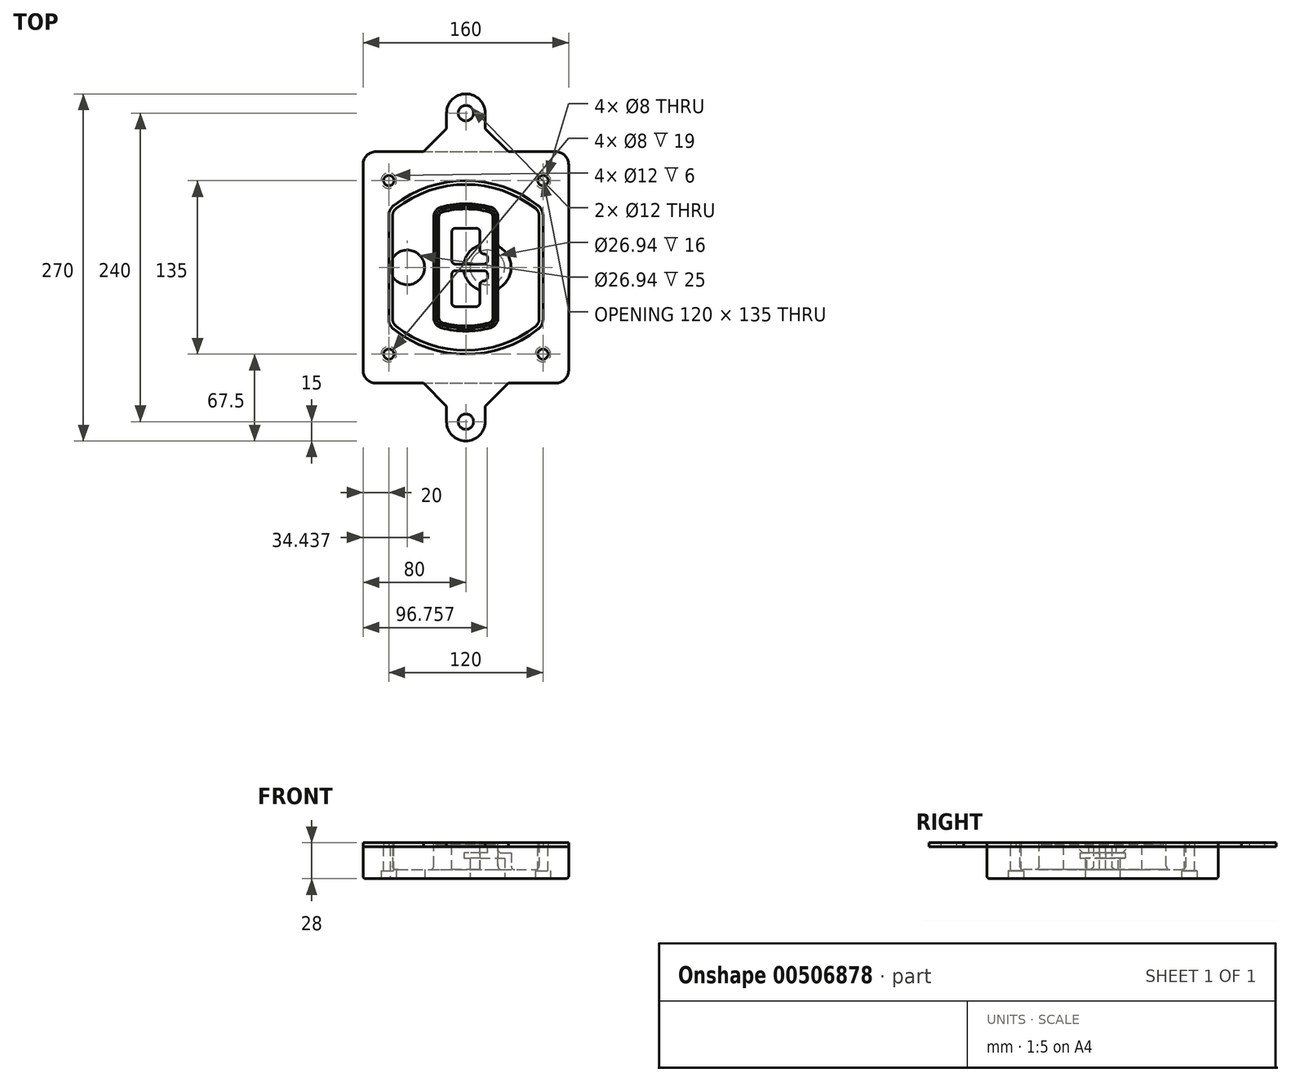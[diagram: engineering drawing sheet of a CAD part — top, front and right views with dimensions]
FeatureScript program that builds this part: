
annotation { "Feature Type Name" : "Feature", "Feature Type Description" : "" }
export const myFeature = defineFeature(function(context is Context, id is Id, definition is map)
    precondition{}
    {
        {
            var Q0;
            Q0=qCreatedBy(makeId("Top.planeOp"),FACE);
            var sketch = newSketch(context, id + "F0", { "sketchPlane" : qUnion([Q0])});
            skPoint(sketch, "E0.rect.middle", {"position": v(0, 0) * mm});
            skLineSegment(sketch, "E1.bottom", {"start": v(-70, -90) * mm, "end": v(70, -90) * mm});
            skLineSegment(sketch, "E1.top", {"start": v(-70, 90) * mm, "end": v(70, 90) * mm});
            skLineSegment(sketch, "E1.left", {"start": v(-80, -80) * mm, "end": v(-80, 80) * mm});
            skLineSegment(sketch, "E1.right", {"start": v(80, -80) * mm, "end": v(80, 80) * mm});
            skLineSegment(sketch, "E2", {"start": v(-80, 90) * mm, "end": v(80, -90) * mm, "construction": true});
            skLineSegment(sketch, "E3", {"start": v(80, 90) * mm, "end": v(-80, -90) * mm, "construction": true});
            skCircle(sketch, "E4", {"center": v(-60, 67.5) * mm, "radius": 4 * mm});
            skCircle(sketch, "E5", {"center": v(60, 67.5) * mm, "radius": 4 * mm});
            skCircle(sketch, "E6", {"center": v(60, -67.5) * mm, "radius": 4 * mm});
            skCircle(sketch, "E7", {"center": v(-60, -67.5) * mm, "radius": 4 * mm});
            skLineSegment(sketch, "E8", {"start": v(-60, 67.5) * mm, "end": v(60, 67.5) * mm, "construction": true});
            skLineSegment(sketch, "E9", {"start": v(60, 67.5) * mm, "end": v(60, -67.5) * mm, "construction": true});
            skLineSegment(sketch, "E10", {"start": v(60, -67.5) * mm, "end": v(-60, -67.5) * mm, "construction": true});
            skLineSegment(sketch, "E11", {"start": v(-60, -67.5) * mm, "end": v(-60, 67.5) * mm, "construction": true});
            skLineSegment(sketch, "E12", {"start": v(-60, 40.3) * mm, "end": v(-60, -40.3) * mm});
            skLineSegment(sketch, "E13", {"start": v(60, 40.3) * mm, "end": v(60, -40.3) * mm});
            skArc(sketch, "E14", {"start": v(56.15, 48.18) * mm, "mid": v(0, 67.5) * mm, "end": v(-56.15, 48.18) * mm});
            skArc(sketch, "E15", {"start": v(-56.15, -48.18) * mm, "mid": v(0, -67.5) * mm, "end": v(56.15, -48.18) * mm});
            skLineSegment(sketch, "E16", {"start": v(-60, 0) * mm, "end": v(60, 0) * mm, "construction": true});
            skPoint(sketch, "E17.visualSharp", {"position": v(-60, -45) * mm});
            skArc(sketch, "E17.filletArc", {"start": v(-60, -40.3) * mm, "mid": v(-58.99, -44.68) * mm, "end": v(-56.15, -48.18) * mm});
            skPoint(sketch, "E18.visualSharp", {"position": v(-60, 45) * mm});
            skArc(sketch, "E18.filletArc", {"start": v(-56.15, 48.18) * mm, "mid": v(-58.99, 44.68) * mm, "end": v(-60, 40.3) * mm});
            skPoint(sketch, "E19.visualSharp", {"position": v(60, 45) * mm});
            skArc(sketch, "E19.filletArc", {"start": v(60, 40.3) * mm, "mid": v(58.99, 44.68) * mm, "end": v(56.15, 48.18) * mm});
            skPoint(sketch, "E20.visualSharp", {"position": v(60, -45) * mm});
            skArc(sketch, "E20.filletArc", {"start": v(56.15, -48.18) * mm, "mid": v(58.99, -44.68) * mm, "end": v(60, -40.3) * mm});
            skPoint(sketch, "E21.visualSharp", {"position": v(-80, 90) * mm});
            skArc(sketch, "E21.filletArc", {"start": v(-70, 90) * mm, "mid": v(-77.07, 87.07) * mm, "end": v(-80, 80) * mm});
            skPoint(sketch, "E22.visualSharp", {"position": v(80, 90) * mm});
            skArc(sketch, "E22.filletArc", {"start": v(80, 80) * mm, "mid": v(77.07, 87.07) * mm, "end": v(70, 90) * mm});
            skPoint(sketch, "E23.visualSharp", {"position": v(80, -90) * mm});
            skArc(sketch, "E23.filletArc", {"start": v(70, -90) * mm, "mid": v(77.07, -87.07) * mm, "end": v(80, -80) * mm});
            skPoint(sketch, "E24.visualSharp", {"position": v(-80, -90) * mm});
            skArc(sketch, "E24.filletArc", {"start": v(-80, -80) * mm, "mid": v(-77.07, -87.07) * mm, "end": v(-70, -90) * mm});
            skArc(sketch, "E25.0", {"start": v(57, 40.3) * mm, "mid": v(56.3, 43.36) * mm, "end": v(54.3, 45.81) * mm});
            skLineSegment(sketch, "E25.1", {"start": v(57, 40.3) * mm, "end": v(57, -40.3) * mm});
            skArc(sketch, "E25.2", {"start": v(54.3, -45.81) * mm, "mid": v(56.3, -43.36) * mm, "end": v(57, -40.3) * mm});
            skArc(sketch, "E25.3", {"start": v(-54.3, -45.81) * mm, "mid": v(0, -64.5) * mm, "end": v(54.3, -45.81) * mm});
            skArc(sketch, "E25.4", {"start": v(-57, -40.3) * mm, "mid": v(-56.3, -43.36) * mm, "end": v(-54.3, -45.81) * mm});
            skArc(sketch, "E25.5", {"start": v(54.3, 45.81) * mm, "mid": v(0, 64.5) * mm, "end": v(-54.3, 45.81) * mm});
            skLineSegment(sketch, "E25.6", {"start": v(-57, 40.3) * mm, "end": v(-57, -40.3) * mm});
            skArc(sketch, "E25.7", {"start": v(-54.3, 45.81) * mm, "mid": v(-56.3, 43.36) * mm, "end": v(-57, 40.3) * mm});
            skArc(sketch, "E26.0", {"start": v(-58.62, 51.33) * mm, "mid": v(-62.58, 46.43) * mm, "end": v(-64, 40.3) * mm});
            skArc(sketch, "E26.1", {"start": v(58.62, 51.33) * mm, "mid": v(0, 71.5) * mm, "end": v(-58.62, 51.33) * mm});
            skArc(sketch, "E26.2", {"start": v(64, 40.3) * mm, "mid": v(62.58, 46.43) * mm, "end": v(58.62, 51.33) * mm});
            skLineSegment(sketch, "E26.3", {"start": v(64, 40.3) * mm, "end": v(64, -40.3) * mm});
            skArc(sketch, "E26.4", {"start": v(58.62, -51.33) * mm, "mid": v(62.58, -46.43) * mm, "end": v(64, -40.3) * mm});
            skLineSegment(sketch, "E26.5", {"start": v(-64, 40.3) * mm, "end": v(-64, -40.3) * mm});
            skArc(sketch, "E26.6", {"start": v(-58.62, -51.33) * mm, "mid": v(0, -71.5) * mm, "end": v(58.62, -51.33) * mm});
            skArc(sketch, "E26.7", {"start": v(-64, -40.3) * mm, "mid": v(-62.58, -46.43) * mm, "end": v(-58.62, -51.33) * mm});
            skSolve(sketch);
        }
        {
            var Q0;
            Q0=makeQuery(id+"F0.imprint","IMPRINT",FACE,{"disambiguationData":[TD([[makeQuery(id+"F0.imprint","IMPRINT",EDGE,{"derivedFrom":sQuery(id+"F0.wireOp",EDGE,"E1.bottom")}),1.0]])]});
            var Q1;
            Q1=makeQuery(id+"F0.imprint","IMPRINT",FACE,{"disambiguationData":[TD([[makeQuery(id+"F0.imprint","IMPRINT",EDGE,{"derivedFrom":sQuery(id+"F0.wireOp",EDGE,"E12")}),1.0]])]});
            var Q2;
            Q2=makeQuery(id+"F0.imprint","IMPRINT",FACE,{"disambiguationData":[TD([[makeQuery(id+"F0.imprint","IMPRINT",EDGE,{"derivedFrom":sQuery(id+"F0.wireOp",EDGE,"E25.0")}),1.0]])]});
            var Q3;
            Q3=makeQuery(id+"F0.imprint","IMPRINT",FACE,{"disambiguationData":[TD([[makeQuery(id+"F0.imprint","IMPRINT",EDGE,{"derivedFrom":sQuery(id+"F0.wireOp",EDGE,"E12")}),-1.0]])]});
            extrude(context, id + "F1", {"entities" : qUnion([Q0, Q1, Q2, Q3]), "oppositeDirection" : true, "depth" : 25 * mm});
        }
        {
            var Q0;
            Q0=makeQuery(id+"F0.imprint","IMPRINT",FACE,{"disambiguationData":[TD([[makeQuery(id+"F0.imprint","IMPRINT",EDGE,{"derivedFrom":sQuery(id+"F0.wireOp",EDGE,"E12")}),1.0]])]});
            extrude(context, id + "F2", {"entities" : qUnion([Q0]), "operationType" : NewBodyOperationType.ADD, "depth" : 3 * mm});
        }
        {
            var Q0;
            Q0=makeQuery(id+"F0.imprint","IMPRINT",FACE,{"disambiguationData":[TD([[makeQuery(id+"F0.imprint","IMPRINT",EDGE,{"derivedFrom":sQuery(id+"F0.wireOp",EDGE,"E25.0")}),1.0]])]});
            extrude(context, id + "F3", {"entities" : qUnion([Q0]), "operationType" : NewBodyOperationType.REMOVE, "oppositeDirection" : true, "depth" : 18 * mm});
        }
        {
            var Q0;
            Q0=makeQuery(id+"F2.opExtrude","CAP_FACE",FACE,{"disambiguationData":[OSD([sQuery(id+"F0.wireOp",EDGE,"E12"),sQuery(id+"F0.wireOp",EDGE,"E13"),sQuery(id+"F0.wireOp",EDGE,"E14"),sQuery(id+"F0.wireOp",EDGE,"E15"),sQuery(id+"F0.wireOp",EDGE,"E17.filletArc"),sQuery(id+"F0.wireOp",EDGE,"E18.filletArc"),sQuery(id+"F0.wireOp",EDGE,"E19.filletArc"),sQuery(id+"F0.wireOp",EDGE,"E20.filletArc"),sQuery(id+"F0.wireOp",EDGE,"E25.0"),sQuery(id+"F0.wireOp",EDGE,"E25.1"),sQuery(id+"F0.wireOp",EDGE,"E25.2"),sQuery(id+"F0.wireOp",EDGE,"E25.3"),sQuery(id+"F0.wireOp",EDGE,"E25.4"),sQuery(id+"F0.wireOp",EDGE,"E25.5"),sQuery(id+"F0.wireOp",EDGE,"E25.6"),sQuery(id+"F0.wireOp",EDGE,"E25.7")])],"isStart":false});
            var sketch = newSketch(context, id + "F4", { "sketchPlane" : qUnion([Q0])});
            skArc(sketch, "E27.0", {"start": v(-19.08, -46.97) * mm, "mid": v(0, -49.5) * mm, "end": v(19.08, -46.97) * mm});
            skArc(sketch, "E28.0", {"start": v(19.08, 46.97) * mm, "mid": v(0, 49.5) * mm, "end": v(-19.08, 46.97) * mm});
            skLineSegment(sketch, "E29", {"start": v(-25, 39.25) * mm, "end": v(-25, -39.25) * mm});
            skLineSegment(sketch, "E30", {"start": v(25, 39.25) * mm, "end": v(25, -39.25) * mm});
            skLineSegment(sketch, "E31", {"start": v(-25, 45.1) * mm, "end": v(25, 45.1) * mm, "construction": true});
            skLineSegment(sketch, "E32", {"start": v(-25, -45.1) * mm, "end": v(25, -45.1) * mm, "construction": true});
            skPoint(sketch, "E33.visualSharp", {"position": v(-25, 45.1) * mm});
            skArc(sketch, "E33.filletArc", {"start": v(-19.08, 46.97) * mm, "mid": v(-23.35, 44.11) * mm, "end": v(-25, 39.25) * mm});
            skPoint(sketch, "E34.visualSharp", {"position": v(25, 45.1) * mm});
            skArc(sketch, "E34.filletArc", {"start": v(25, 39.25) * mm, "mid": v(23.35, 44.11) * mm, "end": v(19.08, 46.97) * mm});
            skPoint(sketch, "E35.visualSharp", {"position": v(25, -45.1) * mm});
            skArc(sketch, "E35.filletArc", {"start": v(19.08, -46.97) * mm, "mid": v(23.35, -44.11) * mm, "end": v(25, -39.25) * mm});
            skPoint(sketch, "E36.visualSharp", {"position": v(-25, -45.1) * mm});
            skArc(sketch, "E36.filletArc", {"start": v(-25, -39.25) * mm, "mid": v(-23.35, -44.11) * mm, "end": v(-19.08, -46.97) * mm});
            skArc(sketch, "E37.0", {"start": v(54.3, 45.81) * mm, "mid": v(0, 64.5) * mm, "end": v(-54.3, 45.81) * mm});
            skArc(sketch, "E37.1", {"start": v(-54.3, 45.81) * mm, "mid": v(-56.3, 43.36) * mm, "end": v(-57, 40.3) * mm});
            skLineSegment(sketch, "E37.2", {"start": v(-57, 40.3) * mm, "end": v(-57, -40.3) * mm});
            skArc(sketch, "E37.3", {"start": v(-57, -40.3) * mm, "mid": v(-56.3, -43.36) * mm, "end": v(-54.3, -45.81) * mm});
            skArc(sketch, "E37.4", {"start": v(-54.3, -45.81) * mm, "mid": v(0, -64.5) * mm, "end": v(54.3, -45.81) * mm});
            skArc(sketch, "E37.5", {"start": v(54.3, -45.81) * mm, "mid": v(56.3, -43.36) * mm, "end": v(57, -40.3) * mm});
            skLineSegment(sketch, "E37.6", {"start": v(57, 40.3) * mm, "end": v(57, -40.3) * mm});
            skArc(sketch, "E37.7", {"start": v(57, 40.3) * mm, "mid": v(56.3, 43.36) * mm, "end": v(54.3, 45.81) * mm});
            skLineSegment(sketch, "E38.0", {"start": v(23, 39.25) * mm, "end": v(23, -39.25) * mm});
            skArc(sketch, "E38.1", {"start": v(18.56, -45.04) * mm, "mid": v(21.76, -42.9) * mm, "end": v(23, -39.25) * mm});
            skArc(sketch, "E38.2", {"start": v(-18.56, -45.04) * mm, "mid": v(0, -47.5) * mm, "end": v(18.56, -45.04) * mm});
            skArc(sketch, "E38.3", {"start": v(-23, -39.25) * mm, "mid": v(-21.76, -42.9) * mm, "end": v(-18.56, -45.04) * mm});
            skLineSegment(sketch, "E38.4", {"start": v(-23, 39.25) * mm, "end": v(-23, -39.25) * mm});
            skArc(sketch, "E38.5", {"start": v(23, 39.25) * mm, "mid": v(21.76, 42.9) * mm, "end": v(18.56, 45.04) * mm});
            skArc(sketch, "E38.6", {"start": v(-18.56, 45.04) * mm, "mid": v(-21.76, 42.9) * mm, "end": v(-23, 39.25) * mm});
            skArc(sketch, "E38.7", {"start": v(18.56, 45.04) * mm, "mid": v(0, 47.5) * mm, "end": v(-18.56, 45.04) * mm});
            skArc(sketch, "E39.0", {"start": v(21, 39.25) * mm, "mid": v(20.18, 41.68) * mm, "end": v(18.04, 43.1) * mm});
            skLineSegment(sketch, "E39.1", {"start": v(21, 39.25) * mm, "end": v(21, -39.25) * mm});
            skArc(sketch, "E39.2", {"start": v(18.04, -43.1) * mm, "mid": v(20.18, -41.68) * mm, "end": v(21, -39.25) * mm});
            skArc(sketch, "E39.3", {"start": v(-18.04, -43.1) * mm, "mid": v(0, -45.5) * mm, "end": v(18.04, -43.1) * mm});
            skArc(sketch, "E39.4", {"start": v(-21, -39.25) * mm, "mid": v(-20.18, -41.68) * mm, "end": v(-18.04, -43.1) * mm});
            skArc(sketch, "E39.5", {"start": v(18.04, 43.1) * mm, "mid": v(0, 45.5) * mm, "end": v(-18.04, 43.1) * mm});
            skLineSegment(sketch, "E39.6", {"start": v(-21, 39.25) * mm, "end": v(-21, -39.25) * mm});
            skArc(sketch, "E39.7", {"start": v(-18.04, 43.1) * mm, "mid": v(-20.18, 41.68) * mm, "end": v(-21, 39.25) * mm});
            skLineSegment(sketch, "E40", {"start": v(-25, 0) * mm, "end": v(25, 0) * mm, "construction": true});
            skLineSegment(sketch, "E41", {"start": v(-11, 5.5) * mm, "end": v(-11, 27.5) * mm});
            skLineSegment(sketch, "E42", {"start": v(-8, 30.5) * mm, "end": v(8, 30.5) * mm});
            skLineSegment(sketch, "E43", {"start": v(11, 27.5) * mm, "end": v(11, 13.5) * mm});
            skLineSegment(sketch, "E44", {"start": v(14, 10.5) * mm, "end": v(14, 10.5) * mm});
            skLineSegment(sketch, "E45", {"start": v(17, 7.5) * mm, "end": v(17, 5.5) * mm});
            skLineSegment(sketch, "E46", {"start": v(14, 2.5) * mm, "end": v(-8, 2.5) * mm});
            skPoint(sketch, "E47.visualSharp", {"position": v(-11, 30.5) * mm});
            skArc(sketch, "E47.filletArc", {"start": v(-8, 30.5) * mm, "mid": v(-10.12, 29.62) * mm, "end": v(-11, 27.5) * mm});
            skPoint(sketch, "E48.visualSharp", {"position": v(11, 30.5) * mm});
            skArc(sketch, "E48.filletArc", {"start": v(11, 27.5) * mm, "mid": v(10.12, 29.62) * mm, "end": v(8, 30.5) * mm});
            skPoint(sketch, "E49.visualSharp", {"position": v(11, 10.5) * mm});
            skArc(sketch, "E49.filletArc", {"start": v(11, 13.5) * mm, "mid": v(11.88, 11.38) * mm, "end": v(14, 10.5) * mm});
            skPoint(sketch, "E50.visualSharp", {"position": v(17, 10.5) * mm});
            skArc(sketch, "E50.filletArc", {"start": v(17, 7.5) * mm, "mid": v(16.12, 9.62) * mm, "end": v(14, 10.5) * mm});
            skPoint(sketch, "E51.visualSharp", {"position": v(17, 2.5) * mm});
            skArc(sketch, "E51.filletArc", {"start": v(14, 2.5) * mm, "mid": v(16.12, 3.38) * mm, "end": v(17, 5.5) * mm});
            skPoint(sketch, "E52.visualSharp", {"position": v(-11, 2.5) * mm});
            skArc(sketch, "E52.filletArc", {"start": v(-11, 5.5) * mm, "mid": v(-10.12, 3.38) * mm, "end": v(-8, 2.5) * mm});
            skLineSegment(sketch, "E53.0.MirrorCS", {"start": v(14, -2.5) * mm, "end": v(-8, -2.5) * mm});
            skArc(sketch, "E54.0.MirrorCS", {"start": v(-11, -5.5) * mm, "mid": v(-10.12, -3.38) * mm, "end": v(-8, -2.5) * mm});
            skLineSegment(sketch, "E55.0.MirrorCS", {"start": v(-11, -5.5) * mm, "end": v(-11, -27.5) * mm});
            skArc(sketch, "E56.0.MirrorCS", {"start": v(-8, -30.5) * mm, "mid": v(-10.12, -29.62) * mm, "end": v(-11, -27.5) * mm});
            skLineSegment(sketch, "E57.0.MirrorCS", {"start": v(-8, -30.5) * mm, "end": v(8, -30.5) * mm});
            skArc(sketch, "E58.0.MirrorCS", {"start": v(11, -27.5) * mm, "mid": v(10.12, -29.62) * mm, "end": v(8, -30.5) * mm});
            skLineSegment(sketch, "E59.0.MirrorCS", {"start": v(11, -27.5) * mm, "end": v(11, -13.5) * mm});
            skArc(sketch, "E60.0.MirrorCS", {"start": v(11, -13.5) * mm, "mid": v(11.88, -11.38) * mm, "end": v(14, -10.5) * mm});
            skArc(sketch, "E61.0.MirrorCS", {"start": v(17, -7.5) * mm, "mid": v(16.12, -9.62) * mm, "end": v(14, -10.5) * mm});
            skLineSegment(sketch, "E62.0.MirrorCS", {"start": v(17, -7.5) * mm, "end": v(17, -5.5) * mm});
            skArc(sketch, "E63.0.MirrorCS", {"start": v(14, -2.5) * mm, "mid": v(16.12, -3.38) * mm, "end": v(17, -5.5) * mm});
            skSolve(sketch);
        }
        {
            var Q0;
            Q0=makeQuery(id+"F4.imprint","IMPRINT",FACE,{"disambiguationData":[TD([[makeQuery(id+"F4.imprint","IMPRINT",EDGE,{"derivedFrom":sQuery(id+"F4.wireOp",EDGE,"E27.0")}),1.0]])]});
            var Q1;
            Q1=makeQuery(id+"F4.imprint","IMPRINT",FACE,{"disambiguationData":[TD([[makeQuery(id+"F4.imprint","IMPRINT",EDGE,{"derivedFrom":sQuery(id+"F4.wireOp",EDGE,"E38.0")}),-1.0]])]});
            var Q2;
            Q2=makeQuery(id+"F4.imprint","IMPRINT",FACE,{"disambiguationData":[TD([[makeQuery(id+"F4.imprint","IMPRINT",EDGE,{"derivedFrom":sQuery(id+"F4.wireOp",EDGE,"E39.0")}),1.0]])]});
            extrude(context, id + "F5", {"entities" : qUnion([Q0, Q1, Q2]), "operationType" : NewBodyOperationType.ADD, "endBound" : BoundingType.UP_TO_NEXT, "oppositeDirection" : true, "depth" : 25 * mm});
        }
        {
            var Q0;
            Q0=makeQuery(id+"F4.imprint","IMPRINT",FACE,{"disambiguationData":[TD([[makeQuery(id+"F4.imprint","IMPRINT",EDGE,{"derivedFrom":sQuery(id+"F4.wireOp",EDGE,"E38.0")}),-1.0]])]});
            extrude(context, id + "F6", {"entities" : qUnion([Q0]), "operationType" : NewBodyOperationType.REMOVE, "oppositeDirection" : true, "depth" : 2 * mm});
        }
        {
            var Q0;
            Q0=makeQuery(id+"F1.opExtrude","CAP_FACE",FACE,{"disambiguationData":[OSD([sQuery(id+"F0.wireOp",EDGE,"E1.bottom"),sQuery(id+"F0.wireOp",EDGE,"E1.top"),sQuery(id+"F0.wireOp",EDGE,"E1.left"),sQuery(id+"F0.wireOp",EDGE,"E1.right"),sQuery(id+"F0.wireOp",EDGE,"E4"),sQuery(id+"F0.wireOp",EDGE,"E5"),sQuery(id+"F0.wireOp",EDGE,"E6"),sQuery(id+"F0.wireOp",EDGE,"E7"),sQuery(id+"F0.wireOp",EDGE,"E21.filletArc"),sQuery(id+"F0.wireOp",EDGE,"E22.filletArc"),sQuery(id+"F0.wireOp",EDGE,"E23.filletArc"),sQuery(id+"F0.wireOp",EDGE,"E24.filletArc")])],"isStart":false});
            var sketch = newSketch(context, id + "F7", { "sketchPlane" : qUnion([Q0])});
            skCircle(sketch, "E64", {"center": v(16.76, 0) * mm, "radius": 13.47 * mm});
            skCircle(sketch, "E65", {"center": v(-45.56, 0) * mm, "radius": 13.47 * mm});
            skLineSegment(sketch, "E66", {"start": v(80, 0) * mm, "end": v(-80, 0) * mm});
            skCircle(sketch, "E67", {"center": v(16.76, 0) * mm, "radius": 18.47 * mm});
            skCircle(sketch, "E68", {"center": v(60, -67.5) * mm, "radius": 6 * mm});
            skCircle(sketch, "E69", {"center": v(-60, -67.5) * mm, "radius": 6 * mm});
            skCircle(sketch, "E70", {"center": v(-60, 67.5) * mm, "radius": 6 * mm});
            skCircle(sketch, "E71", {"center": v(60, 67.5) * mm, "radius": 6 * mm});
            skSolve(sketch);
        }
        {
            var Q0;
            {var subQ1=sQuery(id+"F7.wireOp",EDGE,"E66");var subQ4=sQuery(id+"F7.wireOp",EDGE,"E64");var subQ6=makeQuery(id+"F7.imprint","INTERSECT",VERTEX,{"disambiguationData":[OD(0.0)],"derivedFrom":[subQ4,subQ1]});Q0=makeQuery(id+"F7.imprint","IMPRINT",FACE,{"disambiguationData":[TD([[makeQuery(id+"F7.imprint","IMPRINT",EDGE,{"disambiguationData":[TD([[subQ6,-1.0]])],"derivedFrom":subQ4}),-1.0]])]});}
            var Q1;
            {var subQ0=sQuery(id+"F7.wireOp",EDGE,"E66");var subQ1=sQuery(id+"F7.wireOp",EDGE,"E64");var subQ3=makeQuery(id+"F7.imprint","INTERSECT",VERTEX,{"disambiguationData":[OD(0.0)],"derivedFrom":[subQ1,subQ0]});Q1=makeQuery(id+"F7.imprint","IMPRINT",FACE,{"disambiguationData":[TD([[makeQuery(id+"F7.imprint","IMPRINT",EDGE,{"disambiguationData":[TD([[subQ3,-1.0]])],"derivedFrom":subQ1}),1.0]])]});}
            var Q2;
            {var subQ0=sQuery(id+"F7.wireOp",EDGE,"E66");var subQ1=sQuery(id+"F7.wireOp",EDGE,"E64");var subQ3=makeQuery(id+"F7.imprint","INTERSECT",VERTEX,{"disambiguationData":[OD(0.0)],"derivedFrom":[subQ1,subQ0]});Q2=makeQuery(id+"F7.imprint","IMPRINT",FACE,{"disambiguationData":[TD([[makeQuery(id+"F7.imprint","IMPRINT",EDGE,{"disambiguationData":[TD([[subQ3,1.0]])],"derivedFrom":subQ1}),1.0]])]});}
            var Q3;
            {var subQ1=sQuery(id+"F7.wireOp",EDGE,"E66");var subQ4=sQuery(id+"F7.wireOp",EDGE,"E64");var subQ6=makeQuery(id+"F7.imprint","INTERSECT",VERTEX,{"disambiguationData":[OD(0.0)],"derivedFrom":[subQ4,subQ1]});Q3=makeQuery(id+"F7.imprint","IMPRINT",FACE,{"disambiguationData":[TD([[makeQuery(id+"F7.imprint","IMPRINT",EDGE,{"disambiguationData":[TD([[subQ6,1.0]])],"derivedFrom":subQ4}),-1.0]])]});}
            extrude(context, id + "F8", {"entities" : qUnion([Q0, Q1, Q2, Q3]), "operationType" : NewBodyOperationType.ADD, "oppositeDirection" : true, "depth" : 20 * mm});
        }
        {
            var Q0;
            {var subQ0=sQuery(id+"F7.wireOp",EDGE,"E66");var subQ1=sQuery(id+"F7.wireOp",EDGE,"E64");var subQ3=makeQuery(id+"F7.imprint","INTERSECT",VERTEX,{"disambiguationData":[OD(0.0)],"derivedFrom":[subQ1,subQ0]});Q0=makeQuery(id+"F7.imprint","IMPRINT",FACE,{"disambiguationData":[TD([[makeQuery(id+"F7.imprint","IMPRINT",EDGE,{"disambiguationData":[TD([[subQ3,-1.0]])],"derivedFrom":subQ1}),1.0]])]});}
            var Q1;
            {var subQ0=sQuery(id+"F7.wireOp",EDGE,"E66");var subQ1=sQuery(id+"F7.wireOp",EDGE,"E64");var subQ3=makeQuery(id+"F7.imprint","INTERSECT",VERTEX,{"disambiguationData":[OD(0.0)],"derivedFrom":[subQ1,subQ0]});Q1=makeQuery(id+"F7.imprint","IMPRINT",FACE,{"disambiguationData":[TD([[makeQuery(id+"F7.imprint","IMPRINT",EDGE,{"disambiguationData":[TD([[subQ3,1.0]])],"derivedFrom":subQ1}),1.0]])]});}
            extrude(context, id + "F9", {"entities" : qUnion([Q0, Q1]), "operationType" : NewBodyOperationType.REMOVE, "oppositeDirection" : true, "depth" : 16 * mm});
        }
        {
            var Q0;
            {var subQ0=sQuery(id+"F7.wireOp",EDGE,"E66");var subQ1=sQuery(id+"F7.wireOp",EDGE,"E65");var subQ3=makeQuery(id+"F7.imprint","INTERSECT",VERTEX,{"disambiguationData":[OD(0.0)],"derivedFrom":[subQ1,subQ0]});Q0=makeQuery(id+"F7.imprint","IMPRINT",FACE,{"disambiguationData":[TD([[makeQuery(id+"F7.imprint","IMPRINT",EDGE,{"disambiguationData":[TD([[subQ3,-1.0]])],"derivedFrom":subQ1}),1.0]])]});}
            var Q1;
            {var subQ0=sQuery(id+"F7.wireOp",EDGE,"E66");var subQ1=sQuery(id+"F7.wireOp",EDGE,"E65");var subQ3=makeQuery(id+"F7.imprint","INTERSECT",VERTEX,{"disambiguationData":[OD(0.0)],"derivedFrom":[subQ1,subQ0]});Q1=makeQuery(id+"F7.imprint","IMPRINT",FACE,{"disambiguationData":[TD([[makeQuery(id+"F7.imprint","IMPRINT",EDGE,{"disambiguationData":[TD([[subQ3,1.0]])],"derivedFrom":subQ1}),1.0]])]});}
            extrude(context, id + "F10", {"entities" : qUnion([Q0, Q1]), "operationType" : NewBodyOperationType.REMOVE, "oppositeDirection" : true, "depth" : 25 * mm});
        }
        {
            var Q0;
            Q0=makeQuery(id+"F7.imprint","IMPRINT",FACE,{"disambiguationData":[TD([[makeQuery(id+"F7.imprint","IMPRINT",EDGE,{"derivedFrom":sQuery(id+"F7.wireOp",EDGE,"E68")}),1.0]])]});
            var Q1;
            Q1=makeQuery(id+"F7.imprint","IMPRINT",FACE,{"disambiguationData":[TD([[makeQuery(id+"F7.imprint","IMPRINT",EDGE,{"derivedFrom":makeQuery(id+"F1.opExtrude","CAP_EDGE",EDGE,{"disambiguationData":[OSD([sQuery(id+"F0.wireOp",EDGE,"E5")])],"isStart":false})}),-1.0]])]});
            var Q2;
            Q2=makeQuery(id+"F7.imprint","IMPRINT",FACE,{"disambiguationData":[TD([[makeQuery(id+"F7.imprint","IMPRINT",EDGE,{"derivedFrom":sQuery(id+"F7.wireOp",EDGE,"E69")}),1.0]])]});
            var Q3;
            Q3=makeQuery(id+"F7.imprint","IMPRINT",FACE,{"disambiguationData":[TD([[makeQuery(id+"F7.imprint","IMPRINT",EDGE,{"derivedFrom":makeQuery(id+"F1.opExtrude","CAP_EDGE",EDGE,{"disambiguationData":[OSD([sQuery(id+"F0.wireOp",EDGE,"E4")])],"isStart":false})}),-1.0]])]});
            var Q4;
            Q4=makeQuery(id+"F7.imprint","IMPRINT",FACE,{"disambiguationData":[TD([[makeQuery(id+"F7.imprint","IMPRINT",EDGE,{"derivedFrom":sQuery(id+"F7.wireOp",EDGE,"E70")}),1.0]])]});
            var Q5;
            Q5=makeQuery(id+"F7.imprint","IMPRINT",FACE,{"disambiguationData":[TD([[makeQuery(id+"F7.imprint","IMPRINT",EDGE,{"derivedFrom":makeQuery(id+"F1.opExtrude","CAP_EDGE",EDGE,{"disambiguationData":[OSD([sQuery(id+"F0.wireOp",EDGE,"E7")])],"isStart":false})}),-1.0]])]});
            var Q6;
            Q6=makeQuery(id+"F7.imprint","IMPRINT",FACE,{"disambiguationData":[TD([[makeQuery(id+"F7.imprint","IMPRINT",EDGE,{"derivedFrom":sQuery(id+"F7.wireOp",EDGE,"E71")}),1.0]])]});
            var Q7;
            Q7=makeQuery(id+"F7.imprint","IMPRINT",FACE,{"disambiguationData":[TD([[makeQuery(id+"F7.imprint","IMPRINT",EDGE,{"derivedFrom":makeQuery(id+"F1.opExtrude","CAP_EDGE",EDGE,{"disambiguationData":[OSD([sQuery(id+"F0.wireOp",EDGE,"E6")])],"isStart":false})}),-1.0]])]});
            extrude(context, id + "F11", {"entities" : qUnion([Q0, Q1, Q2, Q3, Q4, Q5, Q6, Q7]), "operationType" : NewBodyOperationType.REMOVE, "oppositeDirection" : true, "depth" : 6 * mm});
        }
        {
            var Q0;
            Q0=makeQuery(id+"F9.boolean.opBoolean","COPY",FACE,{"derivedFrom":makeQuery(id+"F9.opExtrude","CAP_FACE",FACE,{"disambiguationData":[OSD([sQuery(id+"F7.wireOp",EDGE,"E64")])],"isStart":false})});
            var sketch = newSketch(context, id + "F12", { "sketchPlane" : qUnion([Q0])});
            skArc(sketch, "E72.0", {"start": v(11, 17.55) * mm, "mid": v(2.57, 11.82) * mm, "end": v(-1.54, 2.5) * mm});
            skArc(sketch, "E72.1", {"start": v(-1.54, -2.5) * mm, "mid": v(2.57, -11.82) * mm, "end": v(11, -17.55) * mm});
            skLineSegment(sketch, "E73", {"start": v(-1.54, -2.5) * mm, "end": v(14, -2.5) * mm});
            skLineSegment(sketch, "E74.0", {"start": v(14, 2.5) * mm, "end": v(-1.54, 2.5) * mm});
            skArc(sketch, "E74.1", {"start": v(14, 2.5) * mm, "mid": v(16.12, 3.38) * mm, "end": v(17, 5.5) * mm});
            skLineSegment(sketch, "E74.2", {"start": v(17, 7.5) * mm, "end": v(17, 5.5) * mm});
            skArc(sketch, "E74.3", {"start": v(17, 7.5) * mm, "mid": v(16.12, 9.62) * mm, "end": v(14, 10.5) * mm});
            skArc(sketch, "E74.4", {"start": v(11, 13.5) * mm, "mid": v(11.88, 11.38) * mm, "end": v(14, 10.5) * mm});
            skLineSegment(sketch, "E74.5", {"start": v(11, 17.55) * mm, "end": v(11, 13.5) * mm});
            skLineSegment(sketch, "E74.7", {"start": v(14, -2.5) * mm, "end": v(-1.54, -2.5) * mm});
            skArc(sketch, "E74.8", {"start": v(14, -2.5) * mm, "mid": v(16.12, -3.38) * mm, "end": v(17, -5.5) * mm});
            skLineSegment(sketch, "E74.9", {"start": v(17, -7.5) * mm, "end": v(17, -5.5) * mm});
            skArc(sketch, "E74.10", {"start": v(17, -7.5) * mm, "mid": v(16.12, -9.62) * mm, "end": v(14, -10.5) * mm});
            skArc(sketch, "E74.11", {"start": v(11, -13.5) * mm, "mid": v(11.88, -11.38) * mm, "end": v(14, -10.5) * mm});
            skLineSegment(sketch, "E74.12", {"start": v(11, -17.55) * mm, "end": v(11, -13.5) * mm});
            skPoint(sketch, "E75.orphan", {"position": v(11, -27.5) * mm});
            skPoint(sketch, "E76.orphan", {"position": v(-8, -2.5) * mm});
            skPoint(sketch, "E77.orphan", {"position": v(-8, 2.5) * mm});
            skPoint(sketch, "E78.orphan", {"position": v(11, 27.5) * mm});
            skSolve(sketch);
        }
        {
            var Q0;
            {var subQ7=sQuery(id+"F12.wireOp",EDGE,"E72.0");var subQ14=sQuery(id+"F12.wireOp",EDGE,"E72.1");var subQ16=sQuery(id+"F12.wireOp",EDGE,"E74.1");var subQ18=sQuery(id+"F12.wireOp",EDGE,"E74.8");Q0=qUnion([makeQuery(id+"F12.imprint","IMPRINT",FACE,{"disambiguationData":[TD([[makeQuery(id+"F12.imprint","IMPRINT",EDGE,{"derivedFrom":subQ7}),1.0]])]}),makeQuery(id+"F12.imprint","IMPRINT",FACE,{"disambiguationData":[TD([[makeQuery(id+"F12.imprint","IMPRINT",EDGE,{"derivedFrom":subQ14}),1.0]])]}),makeQuery(id+"F12.imprint","IMPRINT",FACE,{"disambiguationData":[TD([[makeQuery(id+"F12.imprint","IMPRINT",EDGE,{"derivedFrom":subQ16}),1.0]])]}),makeQuery(id+"F12.imprint","IMPRINT",FACE,{"disambiguationData":[TD([[makeQuery(id+"F12.imprint","IMPRINT",EDGE,{"derivedFrom":subQ18}),-1.0]])]})]);}
            var Q1;
            Q1=makeQuery(id+"F5.boolean.opBoolean","SPLIT",FACE,{"disambiguationData":[TD([makeQuery(id+"F5.opExtrude","SWEPT_FACE",FACE,{"disambiguationData":[OSD([sQuery(id+"F4.wireOp",EDGE,"E41")])]})])],"derivedFrom":makeQuery(id+"F3.boolean.opBoolean","COPY",FACE,{"derivedFrom":makeQuery(id+"F3.opExtrude","CAP_FACE",FACE,{"disambiguationData":[OSD([sQuery(id+"F0.wireOp",EDGE,"E25.0"),sQuery(id+"F0.wireOp",EDGE,"E25.1"),sQuery(id+"F0.wireOp",EDGE,"E25.2"),sQuery(id+"F0.wireOp",EDGE,"E25.3"),sQuery(id+"F0.wireOp",EDGE,"E25.4"),sQuery(id+"F0.wireOp",EDGE,"E25.5"),sQuery(id+"F0.wireOp",EDGE,"E25.6"),sQuery(id+"F0.wireOp",EDGE,"E25.7")])],"isStart":false})})});
            extrude(context, id + "F13", {"entities" : qUnion([Q0]), "operationType" : NewBodyOperationType.REMOVE, "endBound" : BoundingType.UP_TO_SURFACE, "endBoundEntityFace" : qUnion([Q1]), "depth" : 25 * mm});
        }
        {
            var Q0;
            Q0=makeQuery(id+"F3.boolean.opBoolean","COPY",EDGE,{"derivedFrom":makeQuery(id+"F3.opExtrude","CAP_EDGE",EDGE,{"disambiguationData":[OSD([sQuery(id+"F0.wireOp",EDGE,"E25.6")])],"isStart":false})});
            var Q1;
            Q1=makeQuery(id+"F8.boolean.opBoolean","INTERSECT",EDGE,{"derivedFrom":[makeQuery(id+"F5.opExtrude","SWEPT_FACE",FACE,{"disambiguationData":[OSD([sQuery(id+"F4.wireOp",EDGE,"E30")])]}),makeQuery(id+"F8.opExtrude","CAP_FACE",FACE,{"disambiguationData":[OSD([sQuery(id+"F7.wireOp",EDGE,"E67")])],"isStart":false})]});
            var Q2;
            Q2=makeQuery(id+"F8.boolean.opBoolean","INTERSECT",EDGE,{"disambiguationData":[OD(1.0)],"derivedFrom":[makeQuery(id+"F5.opExtrude","SWEPT_FACE",FACE,{"disambiguationData":[OSD([sQuery(id+"F4.wireOp",EDGE,"E30")])]}),makeQuery(id+"F8.opExtrude","SWEPT_FACE",FACE,{"disambiguationData":[OSD([sQuery(id+"F7.wireOp",EDGE,"E67")])]})]});
            var Q3;
            {var subQ0=sQuery(id+"F4.wireOp",EDGE,"E30");Q3=makeQuery(id+"F8.boolean.opBoolean","SPLIT",EDGE,{"disambiguationData":[TD([makeQuery(id+"F5.opExtrude","SWEPT_FACE",FACE,{"disambiguationData":[OSD([sQuery(id+"F4.wireOp",EDGE,"E35.filletArc")])]})])],"derivedFrom":makeQuery(id+"F5.opExtrude","CAP_EDGE",EDGE,{"disambiguationData":[OSD([subQ0])],"isStart":false})});}
            var Q4;
            {var subQ0=sQuery(id+"F0.wireOp",EDGE,"E25.7");var subQ1=sQuery(id+"F0.wireOp",EDGE,"E25.1");var subQ2=sQuery(id+"F0.wireOp",EDGE,"E25.6");var subQ3=sQuery(id+"F0.wireOp",EDGE,"E25.5");var subQ4=sQuery(id+"F0.wireOp",EDGE,"E25.4");var subQ5=sQuery(id+"F0.wireOp",EDGE,"E25.0");var subQ6=sQuery(id+"F0.wireOp",EDGE,"E25.2");var subQ7=sQuery(id+"F0.wireOp",EDGE,"E25.3");Q4=makeQuery(id+"F8.boolean.opBoolean","INTERSECT",EDGE,{"derivedFrom":[makeQuery(id+"F5.boolean.opBoolean","SPLIT",FACE,{"disambiguationData":[TD([makeQuery(id+"F2.opExtrude","SWEPT_FACE",FACE,{"disambiguationData":[OSD([subQ5])]})])],"derivedFrom":makeQuery(id+"F3.boolean.opBoolean","COPY",FACE,{"derivedFrom":makeQuery(id+"F3.opExtrude","CAP_FACE",FACE,{"disambiguationData":[OSD([subQ5,subQ1,subQ6,subQ7,subQ4,subQ3,subQ2,subQ0])],"isStart":false})})}),makeQuery(id+"F8.opExtrude","SWEPT_FACE",FACE,{"disambiguationData":[OSD([sQuery(id+"F7.wireOp",EDGE,"E67")])]})]});}
            var Q5;
            Q5=makeQuery(id+"F8.boolean.opBoolean","INTERSECT",EDGE,{"disambiguationData":[OD(0.0)],"derivedFrom":[makeQuery(id+"F5.opExtrude","SWEPT_FACE",FACE,{"disambiguationData":[OSD([sQuery(id+"F4.wireOp",EDGE,"E30")])]}),makeQuery(id+"F8.opExtrude","SWEPT_FACE",FACE,{"disambiguationData":[OSD([sQuery(id+"F7.wireOp",EDGE,"E67")])]})]});
            fillet(context, id + "F14", {"entities" : qUnion([Q0, Q1, Q2, Q3, Q4, Q5]), "radius" : 3 * mm, "tangentPropagation" : true, "allowEdgeOverflow" : false});
        }
        {
            var Q0;
            Q0=makeQuery(id+"F1.opExtrude","CAP_EDGE",EDGE,{"disambiguationData":[OSD([sQuery(id+"F0.wireOp",EDGE,"E1.bottom")])],"isStart":false});
            fillet(context, id + "F15", {"entities" : qUnion([Q0]), "radius" : 2 * mm, "tangentPropagation" : true, "allowEdgeOverflow" : false});
        }
        {
            var Q0;
            {var subQ0=sQuery(id+"F0.wireOp",EDGE,"E21.filletArc");var subQ1=sQuery(id+"F0.wireOp",EDGE,"E7");var subQ2=sQuery(id+"F0.wireOp",EDGE,"E6");var subQ3=sQuery(id+"F0.wireOp",EDGE,"E5");var subQ4=sQuery(id+"F0.wireOp",EDGE,"E4");var subQ5=sQuery(id+"F0.wireOp",EDGE,"E22.filletArc");var subQ6=sQuery(id+"F0.wireOp",EDGE,"E1.bottom");var subQ7=sQuery(id+"F0.wireOp",EDGE,"E1.right");var subQ8=sQuery(id+"F0.wireOp",EDGE,"E1.top");var subQ9=sQuery(id+"F0.wireOp",EDGE,"E1.left");var subQ10=sQuery(id+"F0.wireOp",EDGE,"E23.filletArc");var subQ11=sQuery(id+"F0.wireOp",EDGE,"E24.filletArc");Q0=makeQuery(id+"F2.boolean.opBoolean","SPLIT",FACE,{"disambiguationData":[TD([makeQuery(id+"F1.opExtrude","SWEPT_FACE",FACE,{"disambiguationData":[OSD([subQ6])]})])],"derivedFrom":makeQuery(id+"F1.opExtrude","CAP_FACE",FACE,{"disambiguationData":[OSD([subQ6,subQ8,subQ9,subQ7,subQ4,subQ3,subQ2,subQ1,subQ0,subQ5,subQ10,subQ11])],"isStart":true})});}
            var sketch = newSketch(context, id + "F16", { "sketchPlane" : qUnion([Q0])});
            skLineSegment(sketch, "E79.0", {"start": v(-80, -80) * mm, "end": v(-80, 80) * mm});
            skArc(sketch, "E79.1", {"start": v(-70, 90) * mm, "mid": v(-77.07, 87.07) * mm, "end": v(-80, 80) * mm});
            skLineSegment(sketch, "E79.2", {"start": v(-70, 90) * mm, "end": v(70, 90) * mm});
            skArc(sketch, "E79.3", {"start": v(80, 80) * mm, "mid": v(77.07, 87.07) * mm, "end": v(70, 90) * mm});
            skLineSegment(sketch, "E79.4", {"start": v(80, -80) * mm, "end": v(80, 80) * mm});
            skArc(sketch, "E79.5", {"start": v(70, -90) * mm, "mid": v(77.07, -87.07) * mm, "end": v(80, -80) * mm});
            skLineSegment(sketch, "E79.6", {"start": v(-70, -90) * mm, "end": v(70, -90) * mm});
            skArc(sketch, "E79.7", {"start": v(-80, -80) * mm, "mid": v(-77.07, -87.07) * mm, "end": v(-70, -90) * mm});
            skCircle(sketch, "E79.8", {"center": v(-60, -67.5) * mm, "radius": 4 * mm});
            skCircle(sketch, "E79.9", {"center": v(-60, 67.5) * mm, "radius": 4 * mm});
            skCircle(sketch, "E79.10", {"center": v(60, 67.5) * mm, "radius": 4 * mm});
            skCircle(sketch, "E79.11", {"center": v(60, -67.5) * mm, "radius": 4 * mm});
            skArc(sketch, "E79.12", {"start": v(-56.15, -48.18) * mm, "mid": v(0, -67.5) * mm, "end": v(56.15, -48.18) * mm});
            skArc(sketch, "E79.13", {"start": v(56.15, -48.18) * mm, "mid": v(58.99, -44.68) * mm, "end": v(60, -40.3) * mm});
            skLineSegment(sketch, "E79.14", {"start": v(60, 40.3) * mm, "end": v(60, -40.3) * mm});
            skArc(sketch, "E79.15", {"start": v(60, 40.3) * mm, "mid": v(58.99, 44.68) * mm, "end": v(56.15, 48.18) * mm});
            skArc(sketch, "E79.16", {"start": v(56.15, 48.18) * mm, "mid": v(0, 67.5) * mm, "end": v(-56.15, 48.18) * mm});
            skArc(sketch, "E79.17", {"start": v(-56.15, 48.18) * mm, "mid": v(-58.99, 44.68) * mm, "end": v(-60, 40.3) * mm});
            skLineSegment(sketch, "E79.18", {"start": v(-60, 40.3) * mm, "end": v(-60, -40.3) * mm});
            skArc(sketch, "E79.19", {"start": v(-60, -40.3) * mm, "mid": v(-58.99, -44.68) * mm, "end": v(-56.15, -48.18) * mm});
            skLineSegment(sketch, "E80", {"start": v(0, 90) * mm, "end": v(0, 120) * mm, "construction": true});
            skCircle(sketch, "E81", {"center": v(0, 120) * mm, "radius": 6 * mm});
            skLineSegment(sketch, "E82", {"start": v(-33, 90) * mm, "end": v(-15, 108) * mm});
            skLineSegment(sketch, "E83", {"start": v(-15, 108) * mm, "end": v(-15, 120) * mm});
            skLineSegment(sketch, "E84", {"start": v(33, 90) * mm, "end": v(15, 108) * mm});
            skLineSegment(sketch, "E85", {"start": v(15, 108) * mm, "end": v(15, 120) * mm});
            skArc(sketch, "E86", {"start": v(15, 120) * mm, "mid": v(0, 135) * mm, "end": v(-15, 120) * mm});
            skLineSegment(sketch, "E87", {"start": v(-80, 0) * mm, "end": v(80, 0) * mm, "construction": true});
            skArc(sketch, "E88.MirrorCS", {"start": v(15, -120) * mm, "mid": v(0, -135) * mm, "end": v(-15, -120) * mm});
            skLineSegment(sketch, "E89.MirrorCS", {"start": v(15, -108) * mm, "end": v(15, -120) * mm});
            skLineSegment(sketch, "E90.MirrorCS", {"start": v(33, -90) * mm, "end": v(15, -108) * mm});
            skLineSegment(sketch, "E91.MirrorCS", {"start": v(-33, -90) * mm, "end": v(-15, -108) * mm});
            skLineSegment(sketch, "E92.MirrorCS", {"start": v(-15, -108) * mm, "end": v(-15, -120) * mm});
            skLineSegment(sketch, "E93.MirrorCS", {"start": v(0, -90) * mm, "end": v(0, -120) * mm, "construction": true});
            skCircle(sketch, "E94.MirrorC", {"center": v(0, -120) * mm, "radius": 6 * mm});
            skSolve(sketch);
        }
        {
            var Q0;
            Q0 = qSketchRegion(id + "F16", true);
            var Q1;
            {var subQ0=sQuery(id+"F4.wireOp",EDGE,"E36.filletArc");var subQ1=sQuery(id+"F4.wireOp",EDGE,"E35.filletArc");var subQ2=sQuery(id+"F4.wireOp",EDGE,"E34.filletArc");var subQ3=sQuery(id+"F4.wireOp",EDGE,"E33.filletArc");var subQ4=sQuery(id+"F4.wireOp",EDGE,"E27.0");var subQ5=sQuery(id+"F4.wireOp",EDGE,"E30");var subQ6=sQuery(id+"F4.wireOp",EDGE,"E28.0");var subQ7=sQuery(id+"F4.wireOp",EDGE,"E29");Q1=makeQuery(id+"F6.boolean.opBoolean","SPLIT",FACE,{"disambiguationData":[TD([makeQuery(id+"F5.opExtrude","SWEPT_FACE",FACE,{"disambiguationData":[OSD([subQ4])]})])],"derivedFrom":makeQuery(id+"F5.opExtrude","CAP_FACE",FACE,{"disambiguationData":[OSD([subQ4,subQ6,subQ7,subQ5,subQ3,subQ2,subQ1,subQ0,sQuery(id+"F4.wireOp",EDGE,"E41"),sQuery(id+"F4.wireOp",EDGE,"E42"),sQuery(id+"F4.wireOp",EDGE,"E43"),sQuery(id+"F4.wireOp",EDGE,"E45"),sQuery(id+"F4.wireOp",EDGE,"E46"),sQuery(id+"F4.wireOp",EDGE,"E47.filletArc"),sQuery(id+"F4.wireOp",EDGE,"E48.filletArc"),sQuery(id+"F4.wireOp",EDGE,"E49.filletArc"),sQuery(id+"F4.wireOp",EDGE,"E50.filletArc"),sQuery(id+"F4.wireOp",EDGE,"E51.filletArc"),sQuery(id+"F4.wireOp",EDGE,"E52.filletArc"),sQuery(id+"F4.wireOp",EDGE,"E53.0.MirrorCS"),sQuery(id+"F4.wireOp",EDGE,"E54.0.MirrorCS"),sQuery(id+"F4.wireOp",EDGE,"E55.0.MirrorCS"),sQuery(id+"F4.wireOp",EDGE,"E56.0.MirrorCS"),sQuery(id+"F4.wireOp",EDGE,"E57.0.MirrorCS"),sQuery(id+"F4.wireOp",EDGE,"E58.0.MirrorCS"),sQuery(id+"F4.wireOp",EDGE,"E59.0.MirrorCS"),sQuery(id+"F4.wireOp",EDGE,"E60.0.MirrorCS"),sQuery(id+"F4.wireOp",EDGE,"E61.0.MirrorCS"),sQuery(id+"F4.wireOp",EDGE,"E62.0.MirrorCS"),sQuery(id+"F4.wireOp",EDGE,"E63.0.MirrorCS")])],"isStart":true})});}
            extrude(context, id + "F17", {"entities" : qUnion([Q0]), "endBound" : BoundingType.UP_TO_SURFACE, "endBoundEntityFace" : qUnion([Q1]), "depth" : 25 * mm});
        }
    });
